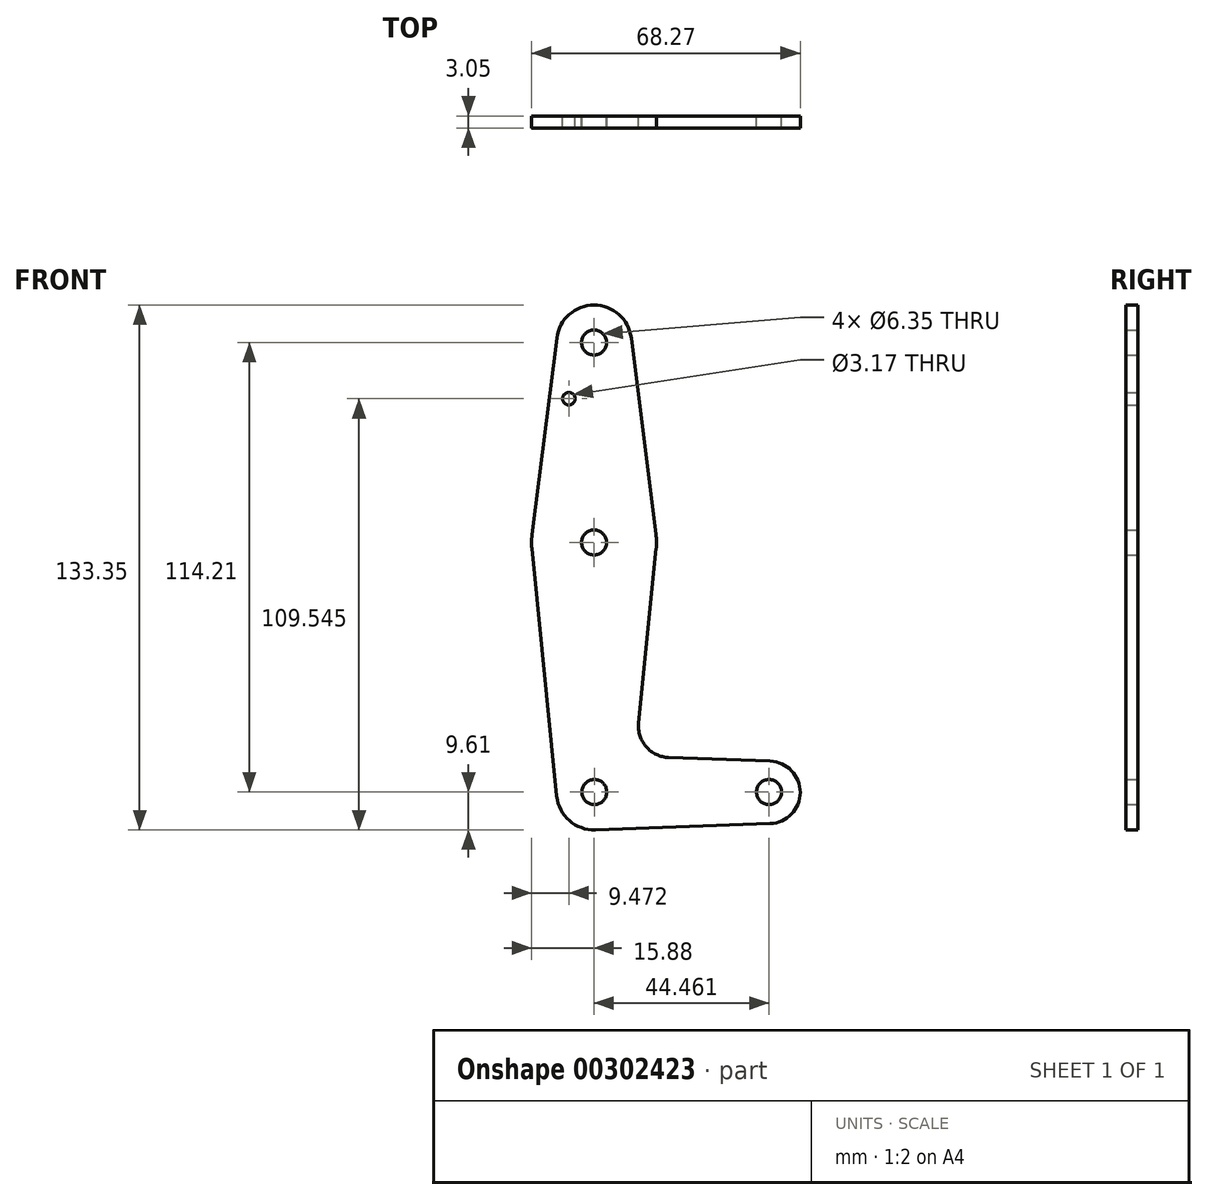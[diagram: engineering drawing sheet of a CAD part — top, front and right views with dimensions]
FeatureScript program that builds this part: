
annotation { "Feature Type Name" : "Feature", "Feature Type Description" : "" }
export const myFeature = defineFeature(function(context is Context, id is Id, definition is map)
    precondition{}
    {
        {
            var Q0;
            Q0=qCreatedBy(makeId("Front.planeOp"),FACE);
            var sketch = newSketch(context, id + "F0", { "sketchPlane" : qUnion([Q0])});
            skCircle(sketch, "E0", {"center": v(0, 0) * mm, "radius": 9.53 * mm});
            skCircle(sketch, "E1", {"center": v(0, 63.5) * mm, "radius": 15.88 * mm});
            skCircle(sketch, "E2", {"center": v(0, 114.3) * mm, "radius": 9.53 * mm});
            skCircle(sketch, "E3", {"center": v(44.45, 0) * mm, "radius": 7.94 * mm});
            skLineSegment(sketch, "E4", {"start": v(0, 114.3) * mm, "end": v(0, 0) * mm, "construction": true});
            skLineSegment(sketch, "E5", {"start": v(44.45, 0) * mm, "end": v(0, 0) * mm, "construction": true});
            skLineSegment(sketch, "E6", {"start": v(-9.45, 115.5) * mm, "end": v(-15.75, 65.48) * mm});
            skLineSegment(sketch, "E7", {"start": v(9.45, 115.5) * mm, "end": v(15.75, 65.48) * mm});
            skLineSegment(sketch, "E8", {"start": v(18.97, 8.85) * mm, "end": v(44.73, 7.93) * mm});
            skLineSegment(sketch, "E9", {"start": v(0.34, -9.52) * mm, "end": v(44.73, -7.93) * mm});
            skLineSegment(sketch, "E10", {"start": v(-15.8, 61.91) * mm, "end": v(-9.48, -0.95) * mm});
            skLineSegment(sketch, "E11", {"start": v(15.8, 61.91) * mm, "end": v(11.34, 17.6) * mm});
            skCircle(sketch, "E12", {"center": v(0, 114.3) * mm, "radius": 3.18 * mm});
            skCircle(sketch, "E13", {"center": v(0, 63.5) * mm, "radius": 3.18 * mm});
            skCircle(sketch, "E14", {"center": v(0.07, 0.09) * mm, "radius": 3.18 * mm});
            skCircle(sketch, "E15", {"center": v(44.46, 0.09) * mm, "radius": 3.18 * mm});
            skCircle(sketch, "E16", {"center": v(-6.4, 100.03) * mm, "radius": 1.59 * mm});
            skArc(sketch, "E17.filletArc", {"start": v(11.34, 17.6) * mm, "mid": v(13.26, 11.57) * mm, "end": v(18.97, 8.85) * mm});
            skSolve(sketch);
        }
        {
            var Q0;
            Q0=qSketchRegion(id+"F0",true);
            extrude(context, id + "F1", {"entities" : qUnion([Q0]), "depth" : 3.05 * mm});
        }
    });
